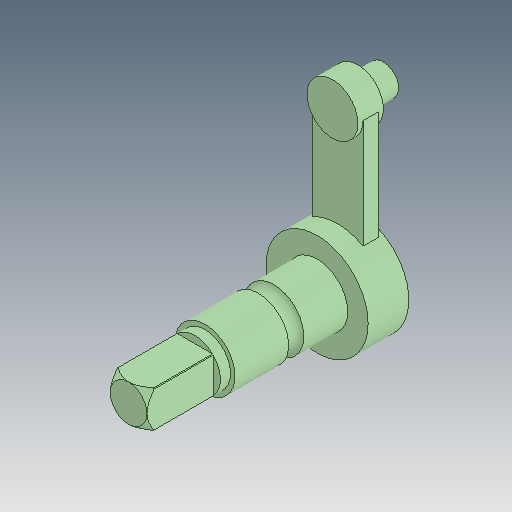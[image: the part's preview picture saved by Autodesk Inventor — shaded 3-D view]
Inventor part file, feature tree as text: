
AUTODESK INVENTOR PART (.ipt)
format: ipt  version: 2017 (Build 210142000, 142)  size: 198,144 bytes
history: native  units: mm
features: sketch x8, extrude x7, other x2, mirror x1, chamfer x1, revolve x1
ambient origin geometry x8: Origin, YZ Plane, XZ Plane, XY Plane, X Axis, Y Axis, Z Axis, Center Point
bodies: Solid1 (feature_tree)
feature tree (20):
  extrude  "Extrusion1"  Depth=6.0mm
  extrude  "Extrusion2"  Depth=10.0mm
  mirror  "Mirror1"
  extrude  "Extrusion3"  Depth=5.0mm TaperAngle=0.0deg
  extrude  "Extrusion4"  Depth=3.0mm TaperAngle=0.0deg
  extrude  "Extrusion5"  Depth=30.0mm TaperAngle=0.0deg
  extrude  "Extrusion6"  Depth=5.0mm TaperAngle=0.0deg
  chamfer  "Chamfer1"  Distance=15.0mm
  extrude  "Extrusion7"  Depth=13.0mm TaperAngle=0.0deg
  other  "Work Point1"
  sketch  "Sketch8"  dims[d18=10.0mm d19=15.0mm d20=0.0mm]
  revolve  "Revolution1"  [1 undecoded]
  sketch  "Sketch1"  dims[d0=30.0mm d1=6.0mm]
  sketch  "Sketch2"  dims[d2=10.0mm d3=12.0mm]
  sketch  "Sketch3"  dims[d4=20.0mm d6=5.0mm d7=0.0mm]
  sketch  "Sketch4"  dims[d8=1.0mm d9=0.0mm d10=3.0mm d11=0.0mm]
  sketch  "Sketch5"  dims[d12=0.1mm d13=30.0mm d14=0.0mm]
  sketch  "Sketch6"  dims[d15=6.0mm d16=5.0mm d17=0.0mm]
  other  "Work Axis1"
  sketch  "Sketch9"  dims[d21=1.4mm d22=2.0mm d23=45.0deg d24=13.0mm d25=0.0mm d26=3.0mm d27=12.0mm d28=90.0deg]
note: 1 required parameter value undecoded (feature->parameter linkage not recoverable at this tier; creation-order binding heuristic only, values carry confidence <= 0.55)
